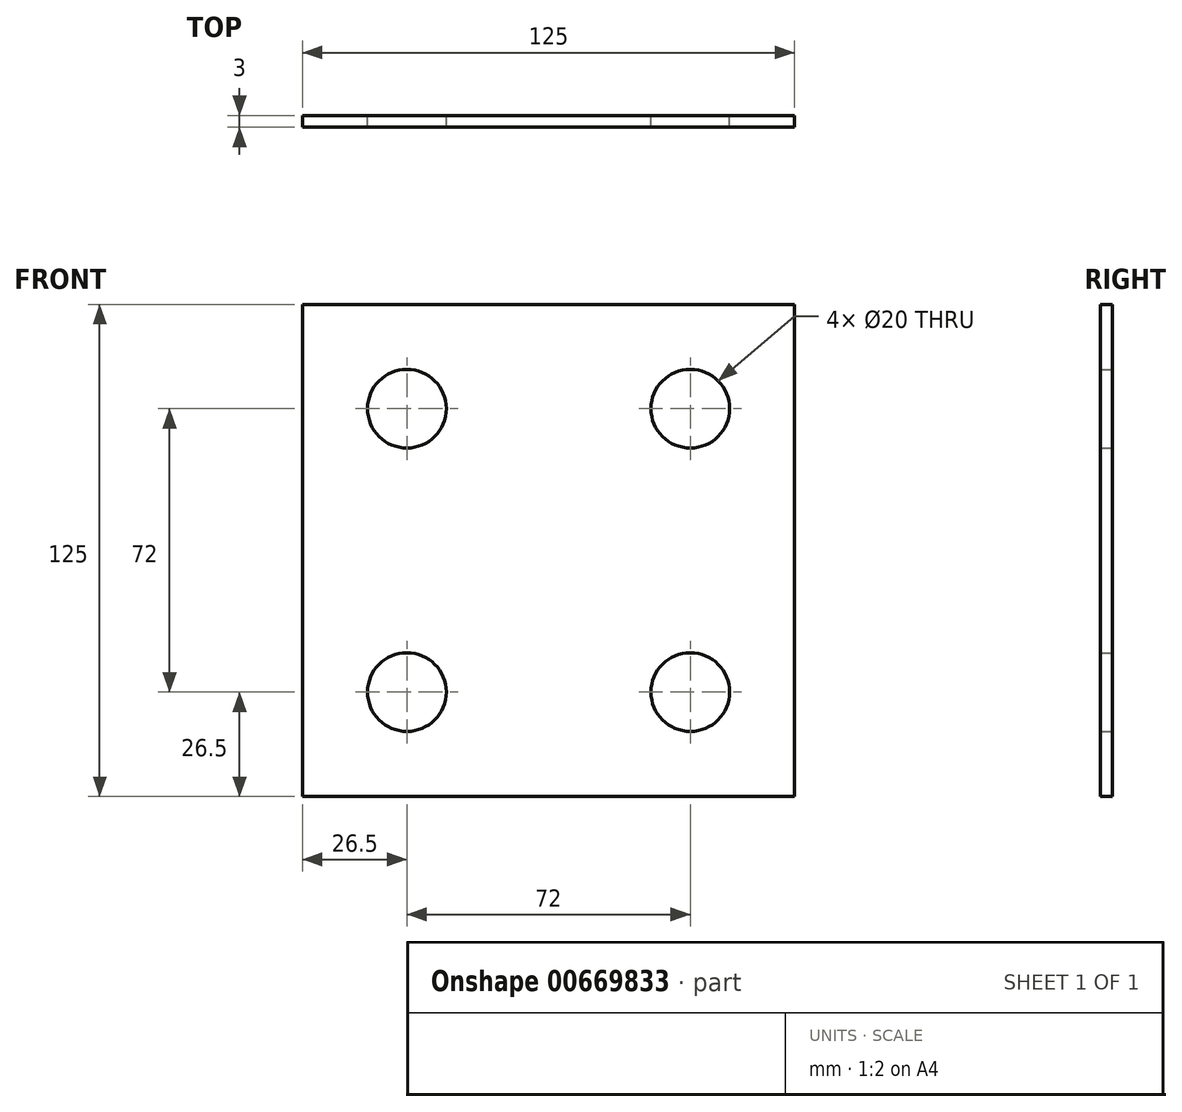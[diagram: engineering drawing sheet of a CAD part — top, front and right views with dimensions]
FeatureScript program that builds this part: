
annotation { "Feature Type Name" : "Feature", "Feature Type Description" : "" }
export const myFeature = defineFeature(function(context is Context, id is Id, definition is map)
    precondition{}
    {
        {
            var Q0;
            Q0=qCreatedBy(makeId("Front.planeOp"),FACE);
            var sketch = newSketch(context, id + "F0", { "sketchPlane" : qUnion([Q0])});
            skLineSegment(sketch, "E0.bottom", {"start": v(-62.5, 62.5) * mm, "end": v(62.5, 62.5) * mm});
            skLineSegment(sketch, "E0.top", {"start": v(-62.5, -62.5) * mm, "end": v(62.5, -62.5) * mm});
            skLineSegment(sketch, "E0.left", {"start": v(-62.5, 62.5) * mm, "end": v(-62.5, -62.5) * mm});
            skLineSegment(sketch, "E0.right", {"start": v(62.5, 62.5) * mm, "end": v(62.5, -62.5) * mm});
            skPoint(sketch, "E0.middle", {"position": v(0, 0) * mm});
            skCircle(sketch, "E1", {"center": v(-36, 36) * mm, "radius": 10 * mm});
            skCircle(sketch, "E2", {"center": v(36, 36) * mm, "radius": 10 * mm});
            skCircle(sketch, "E3", {"center": v(-36, -36) * mm, "radius": 10 * mm});
            skCircle(sketch, "E4", {"center": v(36, -36) * mm, "radius": 10 * mm});
            skLineSegment(sketch, "E5", {"start": v(-36, 36) * mm, "end": v(36, -36) * mm, "construction": true});
            skSolve(sketch);
        }
        {
            var Q0;
            Q0=makeQuery(id+"F0.imprint","IMPRINT",FACE,{"disambiguationData":[TD([[makeQuery(id+"F0.imprint","IMPRINT",EDGE,{"derivedFrom":sQuery(id+"F0.wireOp",EDGE,"E0.bottom")}),-1.0]])]});
            extrude(context, id + "F1", {"entities" : qUnion([Q0]), "depth" : 3 * mm, "offsetDistance" : 25 * mm});
        }
    });
